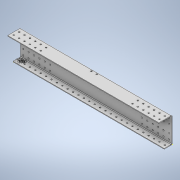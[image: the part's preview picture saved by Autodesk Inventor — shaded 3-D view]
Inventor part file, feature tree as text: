
AUTODESK INVENTOR PART (.ipt)
format: ipt  version: 2022 (Build 260153000, 153)  size: 438,784 bytes
history: native  units: in
note: dims shown in document units (in); Inventor stores cm internally (conversion verified against a paired STEP export)
features: other x8, sheet_metal_op x7, sketch x7, pattern_linear x3
ambient origin geometry x8: Origin, YZ Plane, XZ Plane, XY Plane, X Axis, Y Axis, Z Axis, Center Point
bodies: Solid1 (feature_tree)
feature tree (25):
  sheet_metal_op  "Face1"
  sheet_metal_op  "Flange1"
  sheet_metal_op  "Flange2"
  sketch  "Sketch5"  dims[d3=0.125in]
  pattern_linear  "Rectangular Pattern11"  Spacing1=2.5in  [1 undecoded]
  pattern_linear  "Rectangular Pattern12"  Spacing1=0.5in  [1 undecoded]
  pattern_linear  "Rectangular Pattern14"  Spacing1=0.125in  [1 undecoded]
  sketch  "Sketch1"  dims[d0=28.0in]
  other  "Plate1"
  sketch  "Sketch2"  dims[d1=4.75in]
  other  "Plate2"
  sheet_metal_op  "Bend1"
  sheet_metal_op  "Corner1"
  sketch  "Sketch3"  dims[d2=0.125in]
  other  "Plate3"
  sheet_metal_op  "Bend2"
  sheet_metal_op  "Corner2"
  sketch  "Sketch11"  dims[d4=0.0625in]
  sketch  "Sketch12"  dims[d5=0.25in]
  sketch  "Sketch13"  dims[d6=0.125in d7=2.5in d8=90.0deg d9=0.125in d10=0.5in d11=0.125in d12=0.125in d13=0.125in d14=0.0625in d15=0.25in d16=0.125in d17=1.5in d18=90.0deg d19=0.125in d20=0.5in d21=0.125in d22=0.125in d129=0.26in d177=0.26in d178=0.5in d179=0.26in d180=0.5in d181=0.625in d182=0.26in d183=1.0in d184=0.26in d185=1.5in d186=1.0in d187=0.26in d188=0.625in d189=0.5in d190=0.26in d191=0.26in d192=0.26in d193=1.0in d194=1.5in d195=1.0in d196=0.125in d197=0.0in d198=2.3622in d200=1.0in d201=2.3622in d203=1.0in d204=0.26in d205=0.62in d206=0.5in d207=0.26in d208=1.0in d209=0.5in d210=0.26in d211=0.62in d212=0.5in d213=0.26in d214=1.0in d215=0.5in d216=0.125in d217=0.0in d218=2.3622in d220=1.0in d221=2.3622in d223=1.0in d224=0.26in d225=0.5in d226=0.5in d227=0.26in d228=0.5in d229=0.5in d230=0.125in d231=0.0in d232=0.125in d233=0.0in d237=0.5in d238=0.88in d239=11.0236in d241=1.0in]
  other  "Cut11"
  other  "Cut12"
  other  "Cut13"
  other  "Cut14"
  other  "Definition1"
note: 3 required parameter values undecoded (feature->parameter linkage not recoverable at this tier; creation-order binding heuristic only, values carry confidence <= 0.55)
